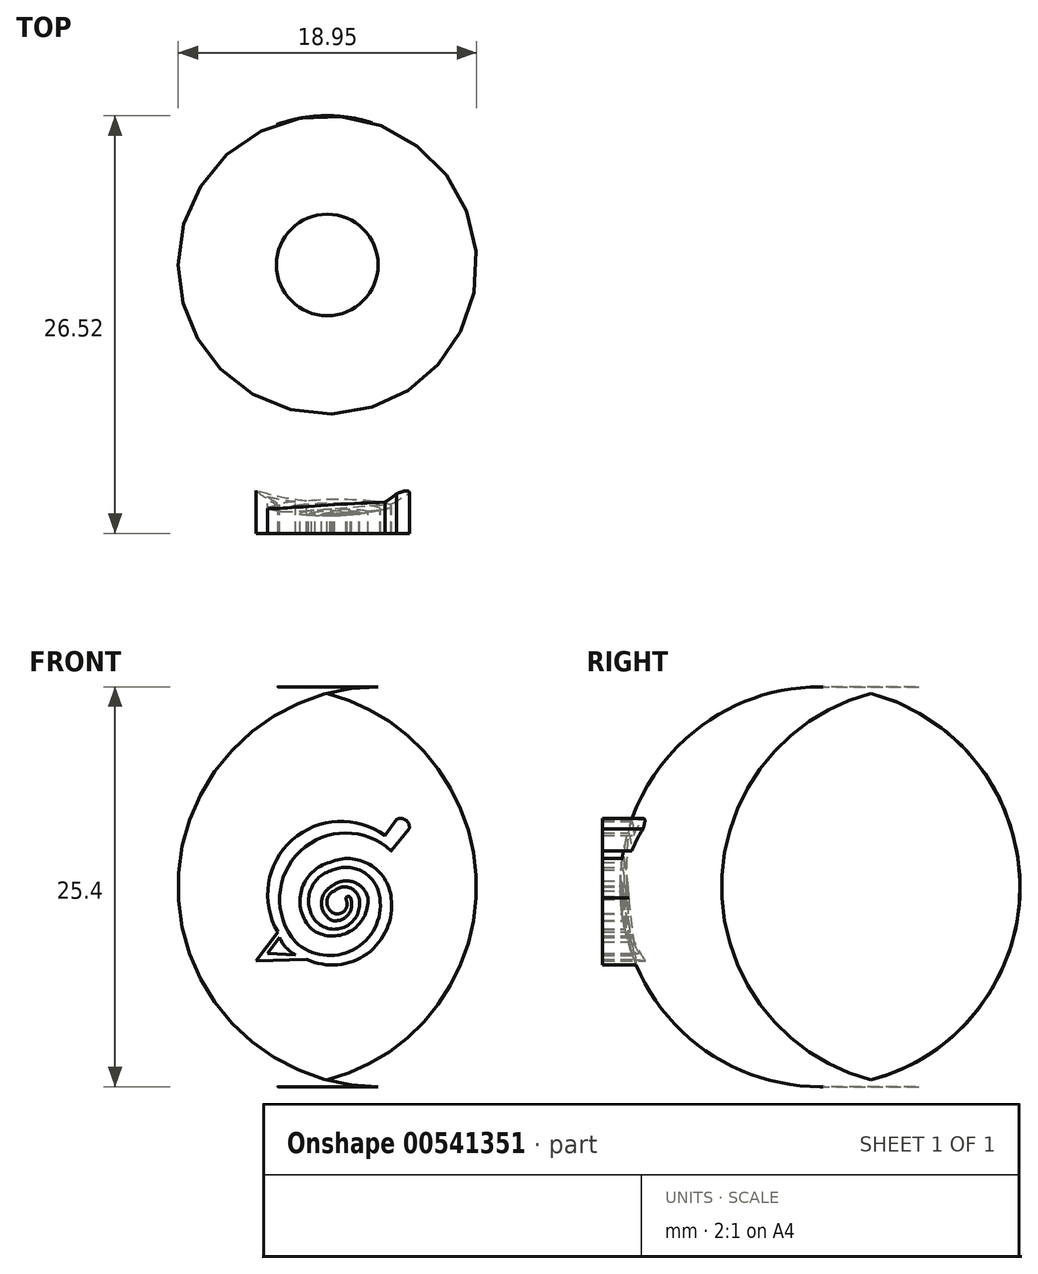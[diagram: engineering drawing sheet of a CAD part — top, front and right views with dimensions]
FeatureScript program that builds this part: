
annotation { "Feature Type Name" : "Feature", "Feature Type Description" : "" }
export const myFeature = defineFeature(function(context is Context, id is Id, definition is map)
    precondition{}
    {
        {
            var Q0;
            Q0=qCreatedBy(makeId("Top.planeOp"),FACE);
            var sketch = newSketch(context, id + "F0", { "sketchPlane" : qUnion([Q0])});
            skCircle(sketch, "E0", {"center": v(-33.08, 17.56) * mm, "radius": 15.93 * mm});
            skSolve(sketch);
        }
        {
            var Q0;
            Q0 = qSketchRegion(id + "F0", true);
            extrude(context, id + "F1", {"entities" : qUnion([Q0]), "depth" : 25.4 * mm, "offsetDistance" : 25.4 * mm});
        }
        {
            var Q0;
            Q0=makeQuery(id+"F1.opExtrude","CAP_EDGE",EDGE,{"disambiguationData":[OSD([sQuery(id+"F0.wireOp",EDGE,"E0")])],"isStart":false});
            var Q1;
            Q1=makeQuery(id+"F1.opExtrude","CAP_EDGE",EDGE,{"disambiguationData":[OSD([sQuery(id+"F0.wireOp",EDGE,"E0")])],"isStart":true});
            fillet(context, id + "F2", {"entities" : qUnion([Q0, Q1]), "radius" : 12.7 * mm, "tangentPropagation" : true, "allowEdgeOverflow" : false});
        }
        {
            var Q0;
            Q0=qCreatedBy(makeId("Front.planeOp"),FACE);
            cPlane(context, id + "F3", {"entities" : qUnion([Q0]), "cplaneType" : CPlaneType.OFFSET, "offset" : 4.32 * mm, "oppositeDirection" : true, "width" : 152.4 * mm, "height" : 152.4 * mm});
        }
        {
            var Q0;
            Q0=qCreatedBy(id+"F3.planeOp",FACE);
            var sketch = newSketch(context, id + "F4", { "sketchPlane" : qUnion([Q0])});
            skArc(sketch, "E1", {"start": v(-27.88, 16.36) * mm, "mid": v(-28.09, 16.93) * mm, "end": v(-28.7, 16.97) * mm});
            skLineSegment(sketch, "E2", {"start": v(-27.88, 16.36) * mm, "end": v(-29.02, 14.97) * mm});
            skLineSegment(sketch, "E3", {"start": v(-28.7, 16.97) * mm, "end": v(-29.42, 15.95) * mm});
            skArc(sketch, "E4", {"start": v(-29.42, 15.95) * mm, "mid": v(-35.32, 15.66) * mm, "end": v(-36.22, 9.83) * mm});
            skArc(sketch, "E5", {"start": v(-34.4, 8.1) * mm, "mid": v(-34.39, 8.1) * mm, "end": v(-34.39, 8.1) * mm});
            skArc(sketch, "E6", {"start": v(-29.02, 11.99) * mm, "mid": v(-30.39, 14.1) * mm, "end": v(-32.9, 14.26) * mm});
            skArc(sketch, "E7", {"start": v(-32.9, 14.26) * mm, "mid": v(-34.72, 12.47) * mm, "end": v(-34.1, 10.01) * mm});
            skArc(sketch, "E8", {"start": v(-34.1, 10.01) * mm, "mid": v(-31.66, 9.85) * mm, "end": v(-30.5, 11.99) * mm});
            skArc(sketch, "E9", {"start": v(-30.5, 11.99) * mm, "mid": v(-31.42, 13) * mm, "end": v(-32.77, 12.74) * mm});
            skArc(sketch, "E10", {"start": v(-32.77, 12.74) * mm, "mid": v(-33.45, 11.65) * mm, "end": v(-32.77, 10.55) * mm});
            skArc(sketch, "E11", {"start": v(-32.77, 10.55) * mm, "mid": v(-31.76, 10.92) * mm, "end": v(-31.61, 11.99) * mm});
            skArc(sketch, "E12", {"start": v(-29.02, 14.97) * mm, "mid": v(-34.8, 14.95) * mm, "end": v(-35.1, 9.18) * mm});
            skArc(sketch, "E13", {"start": v(-35.1, 9.18) * mm, "mid": v(-31.43, 8.7) * mm, "end": v(-29.74, 11.99) * mm});
            skArc(sketch, "E14", {"start": v(-29.74, 11.99) * mm, "mid": v(-30.8, 13.64) * mm, "end": v(-32.75, 13.75) * mm});
            skArc(sketch, "E15", {"start": v(-32.75, 13.75) * mm, "mid": v(-34.16, 12.44) * mm, "end": v(-33.84, 10.55) * mm});
            skArc(sketch, "E16", {"start": v(-33.84, 10.55) * mm, "mid": v(-31.9, 10.18) * mm, "end": v(-31.07, 11.99) * mm});
            skArc(sketch, "E17", {"start": v(-31.07, 11.99) * mm, "mid": v(-31.71, 12.65) * mm, "end": v(-32.61, 12.44) * mm});
            skArc(sketch, "E18", {"start": v(-31.61, 11.99) * mm, "mid": v(-31.8, 12.09) * mm, "end": v(-31.9, 11.9) * mm});
            skLineSegment(sketch, "E19", {"start": v(-36.22, 9.82) * mm, "end": v(-37.6, 8) * mm});
            skLineSegment(sketch, "E20", {"start": v(-37.6, 8) * mm, "end": v(-34.4, 8.1) * mm});
            skArc(sketch, "E21", {"start": v(-34.39, 8.1) * mm, "mid": v(-30.55, 8.45) * mm, "end": v(-29.02, 11.99) * mm});
            skArc(sketch, "E22", {"start": v(-36.22, 9.83) * mm, "mid": v(-36.22, 9.82) * mm, "end": v(-36.22, 9.82) * mm});
            skPoint(sketch, "E23.start.orphan", {"position": v(-32.75, 10.72) * mm});
            skArc(sketch, "E24", {"start": v(-32.61, 12.44) * mm, "mid": v(-33.1, 11.72) * mm, "end": v(-32.61, 11) * mm});
            skArc(sketch, "E25", {"start": v(-32.61, 11) * mm, "mid": v(-31.95, 11.21) * mm, "end": v(-31.9, 11.9) * mm});
            skArc(sketch, "E26", {"start": v(-36.1, 9.49) * mm, "mid": v(-35.71, 8.84) * mm, "end": v(-35.1, 8.38) * mm});
            skLineSegment(sketch, "E27", {"start": v(-36.1, 9.49) * mm, "end": v(-36.87, 8.47) * mm});
            skLineSegment(sketch, "E28", {"start": v(-35.1, 8.38) * mm, "end": v(-36.87, 8.47) * mm});
            skSolve(sketch);
        }
        {
            var Q0;
            Q0 = qSketchRegion(id + "F4", true);
            extrude(context, id + "F5", {"entities" : qUnion([Q0]), "operationType" : NewBodyOperationType.ADD, "depth" : 3.8 * mm, "offsetDistance" : 25.4 * mm});
        }
        {
            var Q0;
            Q0=qCreatedBy(makeId("Right.planeOp"),FACE);
            cPlane(context, id + "F6", {"entities" : qUnion([Q0]), "cplaneType" : CPlaneType.OFFSET, "offset" : 19.3 * mm, "oppositeDirection" : true, "width" : 152.4 * mm, "height" : 152.4 * mm});
        }
    });
